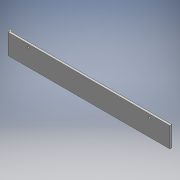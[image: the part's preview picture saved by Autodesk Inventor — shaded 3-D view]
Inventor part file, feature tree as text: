
AUTODESK INVENTOR PART (.ipt)
format: ipt  version: 2016 (Build 200138000, 138)  size: 101,376 bytes
history: native  units: mm
features: sketch x3, extrude x2
ambient origin geometry x8: Origin, YZ Plane, XZ Plane, XY Plane, X Axis, Y Axis, Z Axis, Center Point
bodies: Solid1 (feature_tree)
feature tree (5):
  extrude  "Extrusion1"  Depth=100.0mm
  sketch  "Sketch2"  dims[d3=10.0mm d4=0.0mm d5=10.0mm]
  extrude  "Extrusion2"  Depth=10.0mm
  sketch  "Sketch1"  dims[d0=800.0mm d1=100.0mm]
  sketch  "Sketch3"  dims[d6=10.0mm d7=15.0mm d8=15.0mm d9=100.0mm d10=100.0mm d11=10.0mm d12=0.0mm]
